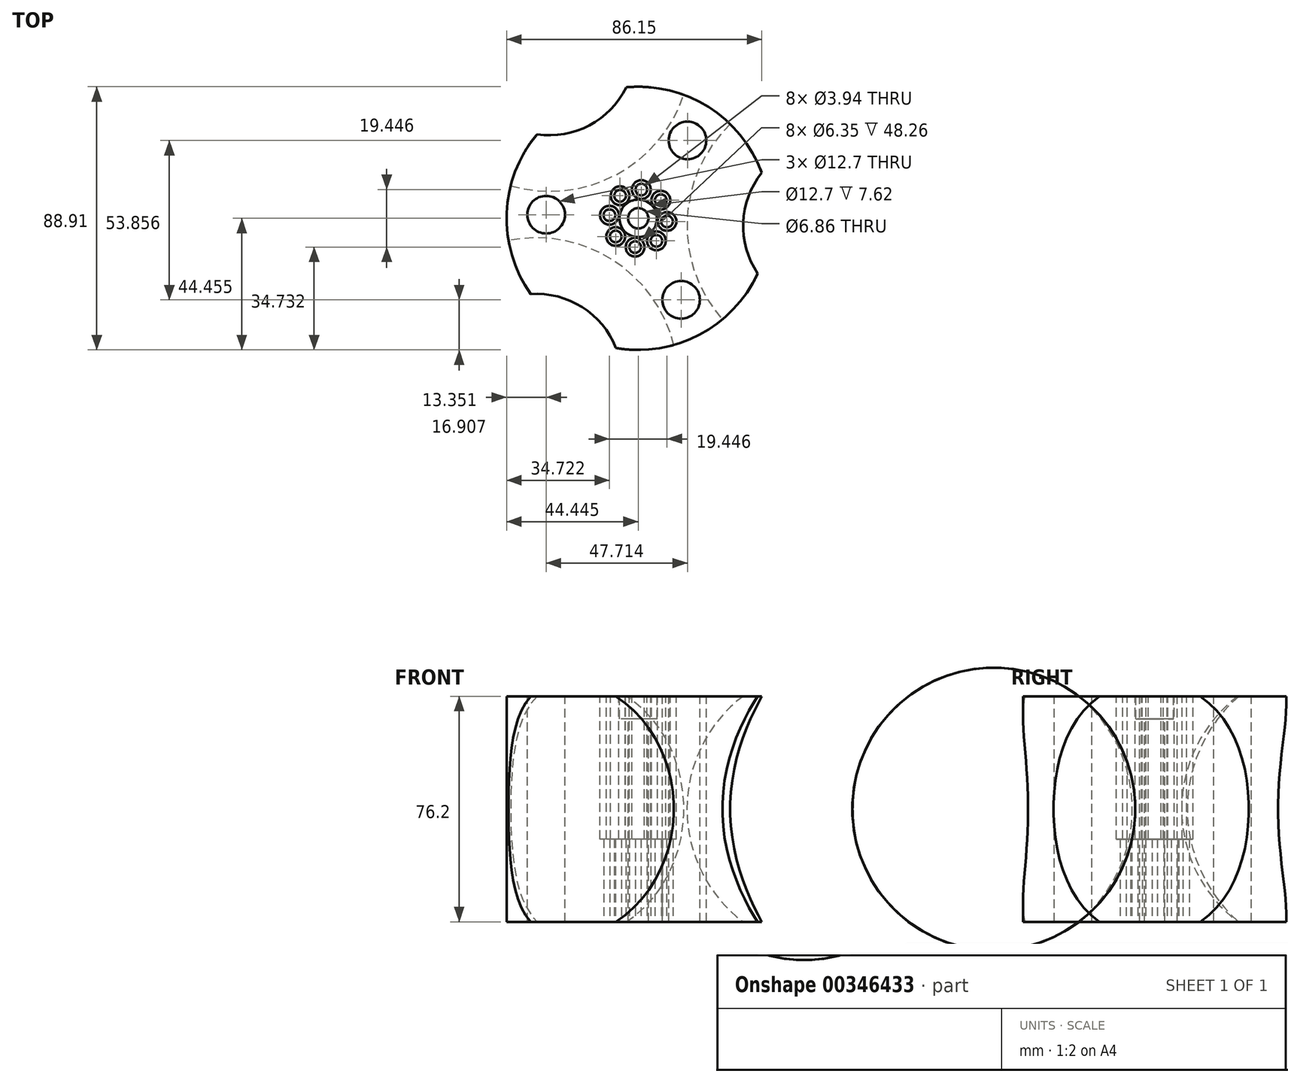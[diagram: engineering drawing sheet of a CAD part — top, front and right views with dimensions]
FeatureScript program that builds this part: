
annotation { "Feature Type Name" : "Feature", "Feature Type Description" : "" }
export const myFeature = defineFeature(function(context is Context, id is Id, definition is map)
    precondition{}
    {
        {
            var Q0;
            Q0=qCreatedBy(makeId("Top.planeOp"),FACE);
            var sketch = newSketch(context, id + "F0", { "sketchPlane" : qUnion([Q0])});
            skCircle(sketch, "E0", {"center": v(-96.8, 47.63) * mm, "radius": 44.45 * mm});
            skCircle(sketch, "E1", {"center": v(-96.8, 47.63) * mm, "radius": 16.51 * mm});
            skCircle(sketch, "E2", {"center": v(-96.8, 47.63) * mm, "radius": 9.78 * mm});
            skCircle(sketch, "E3", {"center": v(-89.18, 53.76) * mm, "radius": 1.97 * mm});
            skCircle(sketch, "E4.1.0", {"center": v(-95.75, 57.35) * mm, "radius": 1.97 * mm});
            skCircle(sketch, "E4.2.0", {"center": v(-102.93, 55.24) * mm, "radius": 1.97 * mm});
            skCircle(sketch, "E4.3.0", {"center": v(-106.52, 48.67) * mm, "radius": 1.97 * mm});
            skCircle(sketch, "E4.4.0", {"center": v(-104.41, 41.5) * mm, "radius": 1.97 * mm});
            skCircle(sketch, "E4.5.0", {"center": v(-97.84, 37.9) * mm, "radius": 1.97 * mm});
            skCircle(sketch, "E4.6.0", {"center": v(-90.66, 40) * mm, "radius": 1.97 * mm});
            skCircle(sketch, "E4.7.0", {"center": v(-87.07, 46.58) * mm, "radius": 1.97 * mm});
            skSolve(sketch);
        }
        {
            var Q0;
            Q0=makeQuery(id+"F0.imprint","IMPRINT",FACE,{"disambiguationData":[TD([[makeQuery(id+"F0.imprint","IMPRINT",EDGE,{"derivedFrom":sQuery(id+"F0.wireOp",EDGE,"E0")}),1.0]])]});
            var Q1;
            Q1=makeQuery(id+"F0.imprint","IMPRINT",FACE,{"disambiguationData":[TD([[makeQuery(id+"F0.imprint","IMPRINT",EDGE,{"derivedFrom":sQuery(id+"F0.wireOp",EDGE,"E1")}),1.0]])]});
            var Q2;
            {var subQ1=sQuery(id+"F0.wireOp",EDGE,"E2");var subQ4=sQuery(id+"F0.wireOp",EDGE,"E3");var subQ5=makeQuery(id+"F0.imprint","INTERSECT",VERTEX,{"disambiguationData":[OD(0.0)],"derivedFrom":[subQ1,subQ4]});Q2=makeQuery(id+"F0.imprint","IMPRINT",FACE,{"disambiguationData":[TD([[makeQuery(id+"F0.imprint","IMPRINT",EDGE,{"disambiguationData":[TD([[subQ5,1.0]])],"derivedFrom":subQ1}),1.0]])]});}
            extrude(context, id + "F1", {"entities" : qUnion([Q0, Q1, Q2]), "depth" : 38.1 * mm, "hasSecondDirection" : true, "secondDirectionOppositeDirection" : true, "secondDirectionDepth" : 38.1 * mm});
        }
        {
            var Q0;
            Q0=qCreatedBy(makeId("Top.planeOp"),FACE);
            var sketch = newSketch(context, id + "F2", { "sketchPlane" : qUnion([Q0])});
            skCircle(sketch, "E5.0.0", {"center": v(-96.8, 47.63) * mm, "radius": 44.45 * mm});
            skCircle(sketch, "E6", {"center": v(-96.8, 47.63) * mm, "radius": 16.51 * mm});
            skLineSegment(sketch, "E7", {"start": v(-107.67, -48.3) * mm, "end": v(-131.12, -6.7) * mm});
            skLineSegment(sketch, "E8", {"start": v(-131.12, -6.7) * mm, "end": v(-154.56, 34.9) * mm});
            skArc(sketch, "E9", {"start": v(-154.56, 34.9) * mm, "mid": v(-172.71, -30.15) * mm, "end": v(-107.67, -48.3) * mm});
            skPoint(sketch, "E10", {"position": v(-80.34, 45.07) * mm});
            skLineSegment(sketch, "E11", {"start": v(-96.8, 47.63) * mm, "end": v(-132.94, -9.59) * mm});
            skLineSegment(sketch, "E12.1.0", {"start": v(-32.58, 45.07) * mm, "end": v(-56.89, 3.96) * mm});
            skArc(sketch, "E12.1.1", {"start": v(-56.89, 3.96) * mm, "mid": v(8.52, 20.77) * mm, "end": v(-8.28, 86.17) * mm});
            skLineSegment(sketch, "E12.1.2", {"start": v(-8.28, 86.17) * mm, "end": v(-32.58, 45.07) * mm});
            skLineSegment(sketch, "E12.2.0", {"start": v(-126.68, 104.51) * mm, "end": v(-78.94, 104.02) * mm});
            skArc(sketch, "E12.2.1", {"start": v(-78.94, 104.02) * mm, "mid": v(-126.2, 152.26) * mm, "end": v(-174.43, 105) * mm});
            skLineSegment(sketch, "E12.2.2", {"start": v(-174.43, 105) * mm, "end": v(-126.68, 104.51) * mm});
            skSolve(sketch);
        }
        {
            var Q0;
            Q0=makeQuery(id+"F2.imprint","IMPRINT",FACE,{"disambiguationData":[TD([[makeQuery(id+"F2.imprint","IMPRINT",EDGE,{"derivedFrom":sQuery(id+"F2.wireOp",EDGE,"E7")}),1.0]])]});
            var Q1;
            Q1=makeQuery(id+"F2.imprint","IMPRINT",FACE,{"disambiguationData":[TD([[makeQuery(id+"F2.imprint","IMPRINT",EDGE,{"derivedFrom":sQuery(id+"F2.wireOp",EDGE,"E12.2.0")}),1.0]])]});
            var Q2;
            Q2=makeQuery(id+"F2.imprint","IMPRINT",FACE,{"disambiguationData":[TD([[makeQuery(id+"F2.imprint","IMPRINT",EDGE,{"derivedFrom":sQuery(id+"F2.wireOp",EDGE,"E12.1.0")}),1.0]])]});
            var Q3;
            Q3=sQuery(id+"F2.wireOp",EDGE,"aOpEJ7Df-Mzx5-U4IW-AKo9-5E0Zru6Bx9m7");
            var Q4;
            Q4=sQuery(id+"F2.wireOp",EDGE,"E12.2.2");
            revolve(context, id + "F3", {"operationType" : NewBodyOperationType.REMOVE, "entities" : qUnion([Q0, Q1, Q2]), "surfaceEntities" : qUnion([Q3]), "axis" : qUnion([Q4]), "revolveType" : RevolveType.FULL, "oppositeDirection" : true});
        }
        {
            var Q0;
            Q0=makeQuery(id+"F2.imprint","IMPRINT",FACE,{"disambiguationData":[TD([[makeQuery(id+"F2.imprint","IMPRINT",EDGE,{"derivedFrom":sQuery(id+"F2.wireOp",EDGE,"E12.1.0")}),1.0]])]});
            var Q1;
            Q1=sQuery(id+"F2.wireOp",EDGE,"E12.1.0");
            revolve(context, id + "F4", {"operationType" : NewBodyOperationType.REMOVE, "entities" : qUnion([Q0]), "axis" : qUnion([Q1]), "revolveType" : RevolveType.FULL, "oppositeDirection" : true});
        }
        {
            var Q0;
            Q0=makeQuery(id+"F2.imprint","IMPRINT",FACE,{"disambiguationData":[TD([[makeQuery(id+"F2.imprint","IMPRINT",EDGE,{"derivedFrom":sQuery(id+"F2.wireOp",EDGE,"E7")}),1.0]])]});
            var Q1;
            Q1=sQuery(id+"F2.wireOp",EDGE,"E7");
            revolve(context, id + "F5", {"operationType" : NewBodyOperationType.REMOVE, "entities" : qUnion([Q0]), "axis" : qUnion([Q1]), "revolveType" : RevolveType.FULL, "oppositeDirection" : true});
        }
        {
            var Q0;
            Q0=makeQuery(id+"F1.opExtrude","CAP_FACE",FACE,{"disambiguationData":[OSD([sQuery(id+"F0.wireOp",EDGE,"E0"),sQuery(id+"F0.wireOp",EDGE,"E3"),sQuery(id+"F0.wireOp",EDGE,"E4.1.0"),sQuery(id+"F0.wireOp",EDGE,"E4.2.0"),sQuery(id+"F0.wireOp",EDGE,"E4.3.0"),sQuery(id+"F0.wireOp",EDGE,"E4.4.0"),sQuery(id+"F0.wireOp",EDGE,"E4.5.0"),sQuery(id+"F0.wireOp",EDGE,"E4.6.0"),sQuery(id+"F0.wireOp",EDGE,"E4.7.0")])],"isStart":false});
            var sketch = newSketch(context, id + "F6", { "sketchPlane" : qUnion([Q0])});
            skCircle(sketch, "E13.0", {"center": v(-102.93, 55.24) * mm, "radius": 1.97 * mm});
            skCircle(sketch, "E14", {"center": v(-102.93, 55.24) * mm, "radius": 3.18 * mm});
            skCircle(sketch, "E15.1.0", {"center": v(-95.75, 57.35) * mm, "radius": 3.18 * mm});
            skCircle(sketch, "E15.2.0", {"center": v(-89.18, 53.76) * mm, "radius": 3.18 * mm});
            skCircle(sketch, "E15.3.0", {"center": v(-87.07, 46.58) * mm, "radius": 3.18 * mm});
            skCircle(sketch, "E15.4.0", {"center": v(-90.66, 40) * mm, "radius": 3.18 * mm});
            skCircle(sketch, "E15.5.0", {"center": v(-97.84, 37.9) * mm, "radius": 3.18 * mm});
            skCircle(sketch, "E15.6.0", {"center": v(-104.41, 41.5) * mm, "radius": 3.18 * mm});
            skCircle(sketch, "E15.7.0", {"center": v(-106.52, 48.67) * mm, "radius": 3.18 * mm});
            skPoint(sketch, "E15.center", {"position": v(-96.8, 47.63) * mm});
            skLineSegment(sketch, "E15.anchor1", {"start": v(-96.8, 47.63) * mm, "end": v(-102.93, 55.24) * mm, "construction": true});
            skLineSegment(sketch, "E15.anchor2", {"start": v(-96.8, 47.63) * mm, "end": v(-106.52, 48.67) * mm, "construction": true});
            skSolve(sketch);
        }
        {
            var Q0;
            Q0=makeQuery(id+"F6.imprint","IMPRINT",FACE,{"disambiguationData":[TD([[makeQuery(id+"F6.imprint","IMPRINT",EDGE,{"derivedFrom":sQuery(id+"F6.wireOp",EDGE,"E13.0")}),-1.0]])]});
            var Q1;
            Q1=makeQuery(id+"F6.imprint","IMPRINT",FACE,{"disambiguationData":[TD([[makeQuery(id+"F6.imprint","IMPRINT",EDGE,{"derivedFrom":sQuery(id+"F6.wireOp",EDGE,"E15.1.0")}),1.0]])]});
            var Q2;
            Q2=makeQuery(id+"F6.imprint","IMPRINT",FACE,{"disambiguationData":[TD([[makeQuery(id+"F6.imprint","IMPRINT",EDGE,{"derivedFrom":sQuery(id+"F6.wireOp",EDGE,"E15.2.0")}),1.0]])]});
            var Q3;
            Q3=makeQuery(id+"F6.imprint","IMPRINT",FACE,{"disambiguationData":[TD([[makeQuery(id+"F6.imprint","IMPRINT",EDGE,{"derivedFrom":sQuery(id+"F6.wireOp",EDGE,"E15.3.0")}),1.0]])]});
            var Q4;
            Q4=makeQuery(id+"F6.imprint","IMPRINT",FACE,{"disambiguationData":[TD([[makeQuery(id+"F6.imprint","IMPRINT",EDGE,{"derivedFrom":sQuery(id+"F6.wireOp",EDGE,"E15.4.0")}),1.0]])]});
            var Q5;
            Q5=makeQuery(id+"F6.imprint","IMPRINT",FACE,{"disambiguationData":[TD([[makeQuery(id+"F6.imprint","IMPRINT",EDGE,{"derivedFrom":sQuery(id+"F6.wireOp",EDGE,"E15.5.0")}),1.0]])]});
            var Q6;
            Q6=makeQuery(id+"F6.imprint","IMPRINT",FACE,{"disambiguationData":[TD([[makeQuery(id+"F6.imprint","IMPRINT",EDGE,{"derivedFrom":sQuery(id+"F6.wireOp",EDGE,"E15.6.0")}),1.0]])]});
            var Q7;
            Q7=makeQuery(id+"F6.imprint","IMPRINT",FACE,{"disambiguationData":[TD([[makeQuery(id+"F6.imprint","IMPRINT",EDGE,{"derivedFrom":sQuery(id+"F6.wireOp",EDGE,"E15.7.0")}),1.0]])]});
            var Q8;
            Q8=sQuery(id+"F6.wireOp",EDGE,"E14");
            var Q9;
            Q9=sQuery(id+"F6.wireOp",EDGE,"E15.1.0");
            var Q10;
            Q10=sQuery(id+"F6.wireOp",EDGE,"E15.2.0");
            var Q11;
            Q11=sQuery(id+"F6.wireOp",EDGE,"E15.3.0");
            var Q12;
            Q12=sQuery(id+"F6.wireOp",EDGE,"E15.4.0");
            var Q13;
            Q13=sQuery(id+"F6.wireOp",EDGE,"E15.5.0");
            var Q14;
            Q14=sQuery(id+"F6.wireOp",EDGE,"E15.6.0");
            var Q15;
            Q15=sQuery(id+"F6.wireOp",EDGE,"E15.7.0");
            extrude(context, id + "F7", {"entities" : qUnion([Q0, Q1, Q2, Q3, Q4, Q5, Q6, Q7]), "operationType" : NewBodyOperationType.REMOVE, "surfaceEntities" : qUnion([Q8, Q9, Q10, Q11, Q12, Q13, Q14, Q15]), "oppositeDirection" : true, "depth" : 48.26 * mm});
        }
        {
            var Q0;
            Q0=makeQuery(id+"F1.opExtrude","CAP_FACE",FACE,{"disambiguationData":[OSD([sQuery(id+"F0.wireOp",EDGE,"E0"),sQuery(id+"F0.wireOp",EDGE,"E3"),sQuery(id+"F0.wireOp",EDGE,"E4.1.0"),sQuery(id+"F0.wireOp",EDGE,"E4.2.0"),sQuery(id+"F0.wireOp",EDGE,"E4.3.0"),sQuery(id+"F0.wireOp",EDGE,"E4.4.0"),sQuery(id+"F0.wireOp",EDGE,"E4.5.0"),sQuery(id+"F0.wireOp",EDGE,"E4.6.0"),sQuery(id+"F0.wireOp",EDGE,"E4.7.0")])],"isStart":false});
            var sketch = newSketch(context, id + "F8", { "sketchPlane" : qUnion([Q0])});
            skCircle(sketch, "E16", {"center": v(-96.8, 47.63) * mm, "radius": 6.35 * mm});
            skSolve(sketch);
        }
        {
            var Q0;
            Q0 = qSketchRegion(id + "F8", true);
            extrude(context, id + "F9", {"entities" : qUnion([Q0]), "operationType" : NewBodyOperationType.REMOVE, "oppositeDirection" : true, "depth" : 7.62 * mm});
        }
        {
            var Q0;
            Q0=makeQuery(id+"F9.boolean.opBoolean","COPY",FACE,{"derivedFrom":makeQuery(id+"F9.opExtrude","CAP_FACE",FACE,{"disambiguationData":[OSD([sQuery(id+"F8.wireOp",EDGE,"E16")])],"isStart":false})});
            var sketch = newSketch(context, id + "F10", { "sketchPlane" : qUnion([Q0])});
            skCircle(sketch, "E17", {"center": v(-96.8, 47.63) * mm, "radius": 3.43 * mm});
            skSolve(sketch);
        }
        {
            var Q0;
            Q0=makeQuery(id+"F10.imprint","IMPRINT",FACE,{"disambiguationData":[TD([[makeQuery(id+"F10.imprint","IMPRINT",EDGE,{"derivedFrom":sQuery(id+"F10.wireOp",EDGE,"E17")}),1.0]])]});
            extrude(context, id + "F11", {"entities" : qUnion([Q0]), "operationType" : NewBodyOperationType.REMOVE, "endBound" : BoundingType.UP_TO_NEXT, "oppositeDirection" : true, "depth" : 25.4 * mm});
        }
        {
            var Q0;
            Q0=makeQuery(id+"F1.opExtrude","CAP_FACE",FACE,{"disambiguationData":[OSD([sQuery(id+"F0.wireOp",EDGE,"E0"),sQuery(id+"F0.wireOp",EDGE,"E3"),sQuery(id+"F0.wireOp",EDGE,"E4.1.0"),sQuery(id+"F0.wireOp",EDGE,"E4.2.0"),sQuery(id+"F0.wireOp",EDGE,"E4.3.0"),sQuery(id+"F0.wireOp",EDGE,"E4.4.0"),sQuery(id+"F0.wireOp",EDGE,"E4.5.0"),sQuery(id+"F0.wireOp",EDGE,"E4.6.0"),sQuery(id+"F0.wireOp",EDGE,"E4.7.0")])],"isStart":false});
            var sketch = newSketch(context, id + "F12", { "sketchPlane" : qUnion([Q0])});
            skLineSegment(sketch, "E18", {"start": v(-96.8, 47.63) * mm, "end": v(-73.05, 85.2) * mm});
            skCircle(sketch, "E19", {"center": v(-80.17, 73.93) * mm, "radius": 6.35 * mm});
            skCircle(sketch, "E20.1.0", {"center": v(-127.89, 48.86) * mm, "radius": 6.35 * mm});
            skCircle(sketch, "E20.2.0", {"center": v(-82.32, 20.08) * mm, "radius": 6.35 * mm});
            skPoint(sketch, "E20.center", {"position": v(-96.8, 47.63) * mm});
            skSolve(sketch);
        }
        {
            var Q0;
            Q0=makeQuery(id+"F12.imprint","IMPRINT",FACE,{"disambiguationData":[TD([[makeQuery(id+"F12.imprint","IMPRINT",EDGE,{"derivedFrom":sQuery(id+"F12.wireOp",EDGE,"E20.1.0")}),1.0]])]});
            var Q1;
            {var subQ0=sQuery(id+"F12.wireOp",EDGE,"E19");var subQ1=sQuery(id+"F12.wireOp",EDGE,"E18");var subQ2=makeQuery(id+"F12.imprint","INTERSECT",VERTEX,{"disambiguationData":[OD(0.0)],"derivedFrom":[subQ1,subQ0]});Q1=makeQuery(id+"F12.imprint","IMPRINT",FACE,{"disambiguationData":[TD([[makeQuery(id+"F12.imprint","IMPRINT",EDGE,{"disambiguationData":[TD([[subQ2,-1.0]])],"derivedFrom":subQ1}),1.0]])]});}
            var Q2;
            {var subQ0=sQuery(id+"F12.wireOp",EDGE,"E19");var subQ1=sQuery(id+"F12.wireOp",EDGE,"E18");var subQ2=makeQuery(id+"F12.imprint","INTERSECT",VERTEX,{"disambiguationData":[OD(0.0)],"derivedFrom":[subQ1,subQ0]});Q2=makeQuery(id+"F12.imprint","IMPRINT",FACE,{"disambiguationData":[TD([[makeQuery(id+"F12.imprint","IMPRINT",EDGE,{"disambiguationData":[TD([[subQ2,-1.0]])],"derivedFrom":subQ1}),-1.0]])]});}
            var Q3;
            Q3=makeQuery(id+"F12.imprint","IMPRINT",FACE,{"disambiguationData":[TD([[makeQuery(id+"F12.imprint","IMPRINT",EDGE,{"derivedFrom":sQuery(id+"F12.wireOp",EDGE,"E20.2.0")}),1.0]])]});
            extrude(context, id + "F13", {"entities" : qUnion([Q0, Q1, Q2, Q3]), "operationType" : NewBodyOperationType.REMOVE, "endBound" : BoundingType.UP_TO_NEXT, "oppositeDirection" : true, "depth" : 25.4 * mm});
        }
    });
